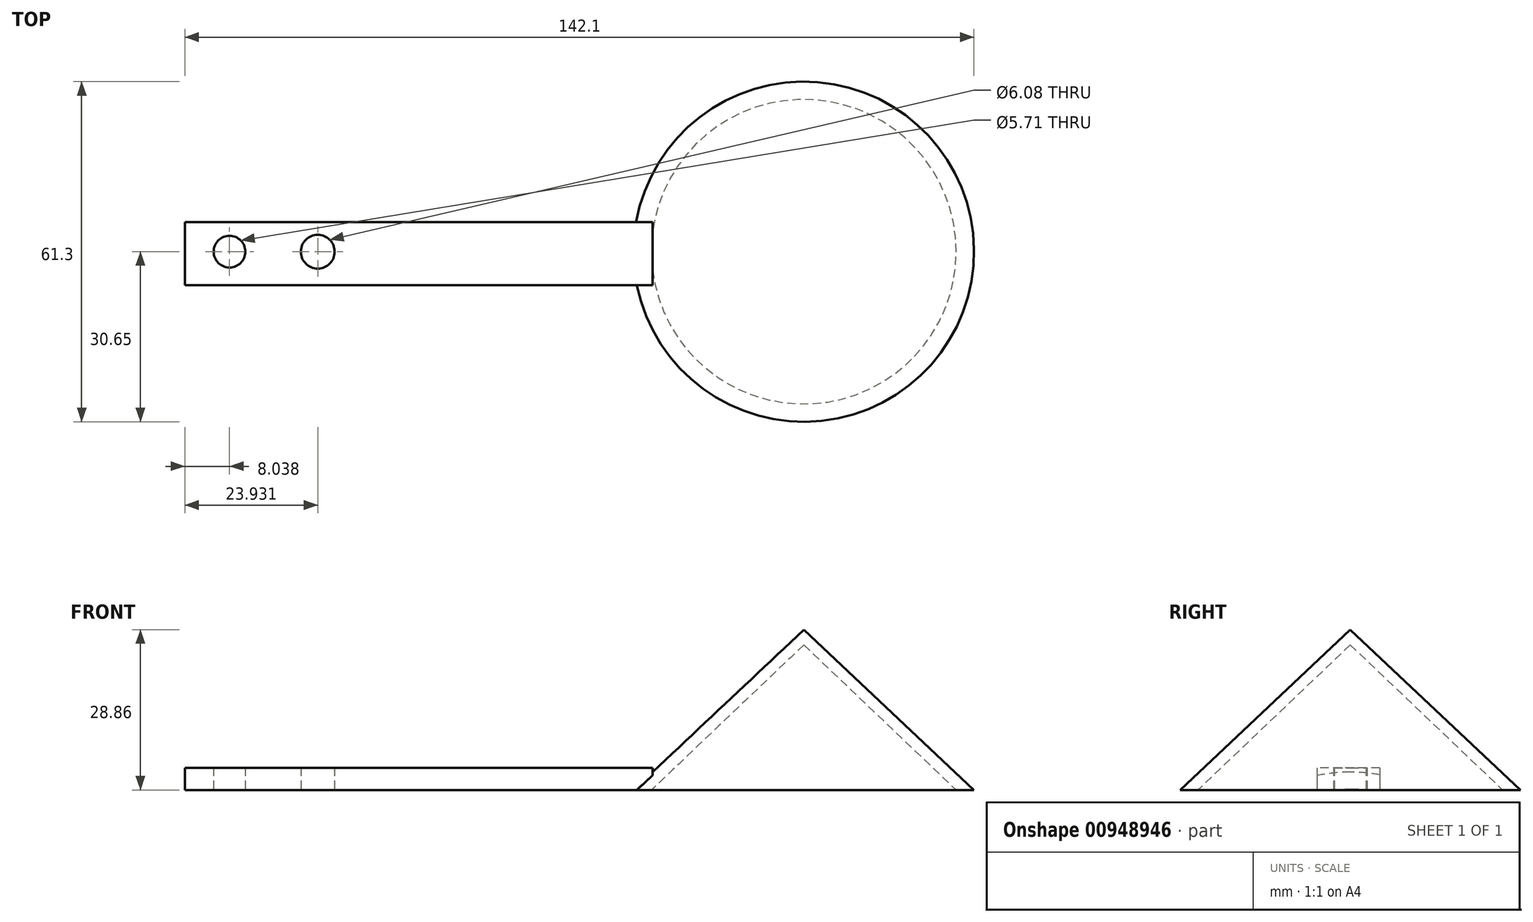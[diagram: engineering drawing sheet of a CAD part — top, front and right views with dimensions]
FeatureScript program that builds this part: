
annotation { "Feature Type Name" : "Feature", "Feature Type Description" : "" }
export const myFeature = defineFeature(function(context is Context, id is Id, definition is map)
    precondition{}
    {
        {
            var Q0;
            Q0=qCreatedBy(makeId("Front.planeOp"),FACE);
            var sketch = newSketch(context, id + "F0", { "sketchPlane" : qUnion([Q0])});
            skLineSegment(sketch, "E0", {"start": v(0, 26.13) * mm, "end": v(27.43, 0) * mm});
            skLineSegment(sketch, "E1", {"start": v(27.43, 0) * mm, "end": v(30.65, 0) * mm});
            skLineSegment(sketch, "E2", {"start": v(30.65, 0) * mm, "end": v(0, 28.86) * mm});
            skLineSegment(sketch, "E3", {"start": v(0, 28.86) * mm, "end": v(0, 26.13) * mm});
            skLineSegment(sketch, "E4", {"start": v(0, 26.13) * mm, "end": v(0, 0) * mm});
            skSolve(sketch);
        }
        {
            var Q0;
            Q0=makeQuery(id+"F0.imprint","IMPRINT",FACE,{"disambiguationData":[TD([[makeQuery(id+"F0.imprint","IMPRINT",EDGE,{"derivedFrom":sQuery(id+"F0.wireOp",EDGE,"E0")}),1.0]])]});
            var Q1;
            Q1=sQuery(id+"F0.wireOp",EDGE,"E4");
            revolve(context, id + "F1", {"surfaceOperationType" : NewSurfaceOperationType.NEW, "entities" : qUnion([Q0]), "axis" : qUnion([Q1]), "revolveType" : RevolveType.FULL});
        }
        {
            var Q0;
            Q0=qCreatedBy(makeId("Top.planeOp"),FACE);
            var sketch = newSketch(context, id + "F2", { "sketchPlane" : qUnion([Q0])});
            skLineSegment(sketch, "E5.bottom", {"start": v(-27.24, 5.3) * mm, "end": v(-111.45, 5.3) * mm});
            skLineSegment(sketch, "E5.top", {"start": v(-27.24, -6.03) * mm, "end": v(-111.45, -6.03) * mm});
            skLineSegment(sketch, "E5.left", {"start": v(-27.24, 5.3) * mm, "end": v(-27.24, -6.03) * mm});
            skLineSegment(sketch, "E5.right", {"start": v(-111.45, 5.3) * mm, "end": v(-111.45, -6.03) * mm});
            skCircle(sketch, "E6", {"center": v(-103.41, 0) * mm, "radius": 2.86 * mm});
            skCircle(sketch, "E7", {"center": v(-87.52, 0) * mm, "radius": 3.04 * mm});
            skSolve(sketch);
        }
        {
            var Q0;
            Q0=makeQuery(id+"F2.imprint","IMPRINT",FACE,{"disambiguationData":[TD([[makeQuery(id+"F2.imprint","IMPRINT",EDGE,{"derivedFrom":sQuery(id+"F2.wireOp",EDGE,"E5.bottom")}),1.0]])]});
            extrude(context, id + "F3", {"entities" : qUnion([Q0]), "operationType" : NewBodyOperationType.ADD, "depth" : 4 * mm, "offsetDistance" : 25 * mm});
        }
    });
